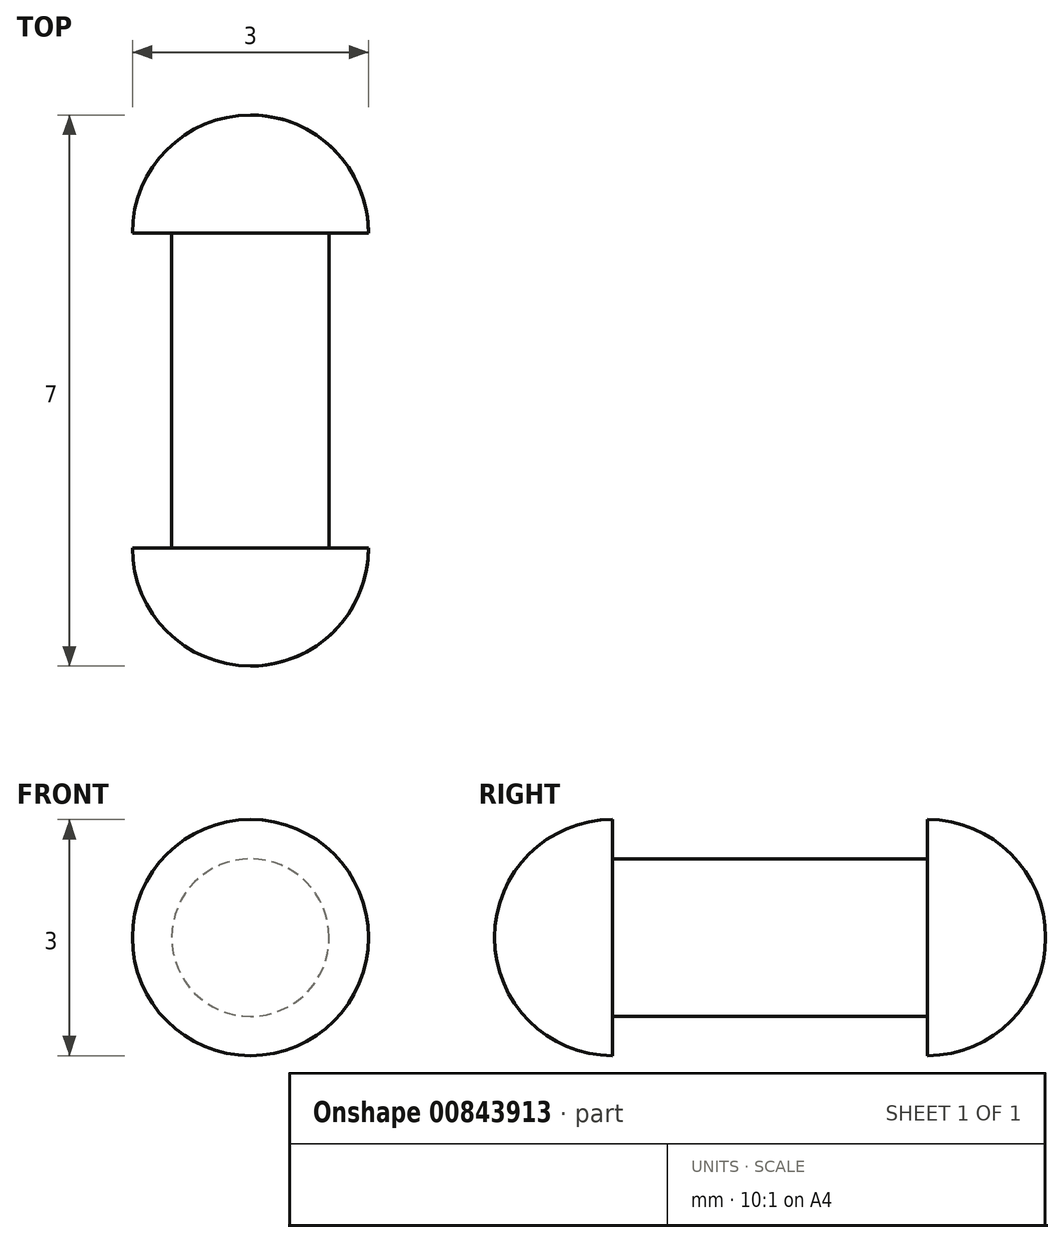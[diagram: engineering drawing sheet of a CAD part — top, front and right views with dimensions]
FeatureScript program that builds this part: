
annotation { "Feature Type Name" : "Feature", "Feature Type Description" : "" }
export const myFeature = defineFeature(function(context is Context, id is Id, definition is map)
    precondition{}
    {
        {
            var Q0;
            Q0=qCreatedBy(makeId("Front.planeOp"),FACE);
            var sketch = newSketch(context, id + "F0", { "sketchPlane" : qUnion([Q0])});
            skCircle(sketch, "E0", {"center": v(0, 0) * mm, "radius": 1 * mm});
            skSolve(sketch);
        }
        {
            var Q0;
            Q0 = qSketchRegion(id + "F0", true);
            extrude(context, id + "F1", {"entities" : qUnion([Q0]), "endBound" : BoundingType.SYMMETRIC, "depth" : 4 * mm, "offsetDistance" : 25 * mm});
        }
        {
            var Q0;
            Q0=qCreatedBy(makeId("Top.planeOp"),FACE);
            var sketch = newSketch(context, id + "F2", { "sketchPlane" : qUnion([Q0])});
            skArc(sketch, "E1", {"start": v(1.5, 2) * mm, "mid": v(1.06, 3.06) * mm, "end": v(0, 3.5) * mm});
            skLineSegment(sketch, "E2", {"start": v(0, 2) * mm, "end": v(1.5, 2) * mm});
            skLineSegment(sketch, "E3", {"start": v(0, 2) * mm, "end": v(0, 3.5) * mm});
            skSolve(sketch);
        }
        {
            var Q0;
            Q0 = qSketchRegion(id + "F2", true);
            var Q1;
            Q1=sQuery(id+"F2.wireOp",EDGE,"E3");
            revolve(context, id + "F3", {"operationType" : NewBodyOperationType.ADD, "surfaceOperationType" : NewSurfaceOperationType.NEW, "entities" : qUnion([Q0]), "axis" : qUnion([Q1]), "revolveType" : RevolveType.FULL});
        }
        {
            var Q0;
            Q0=makeQuery(id+"F1.opExtrude","SWEPT_BODY",BODY,{"disambiguationData":[OSD([sQuery(id+"F0.wireOp",EDGE,"E0")])]});
            var Q1;
            Q1=qCreatedBy(makeId("Front.planeOp"),FACE);
            mirror(context, id + "F4", {"operationType" : NewBodyOperationType.ADD, "entities" : qUnion([Q0]), "mirrorPlane" : qUnion([Q1])});
        }
    });
